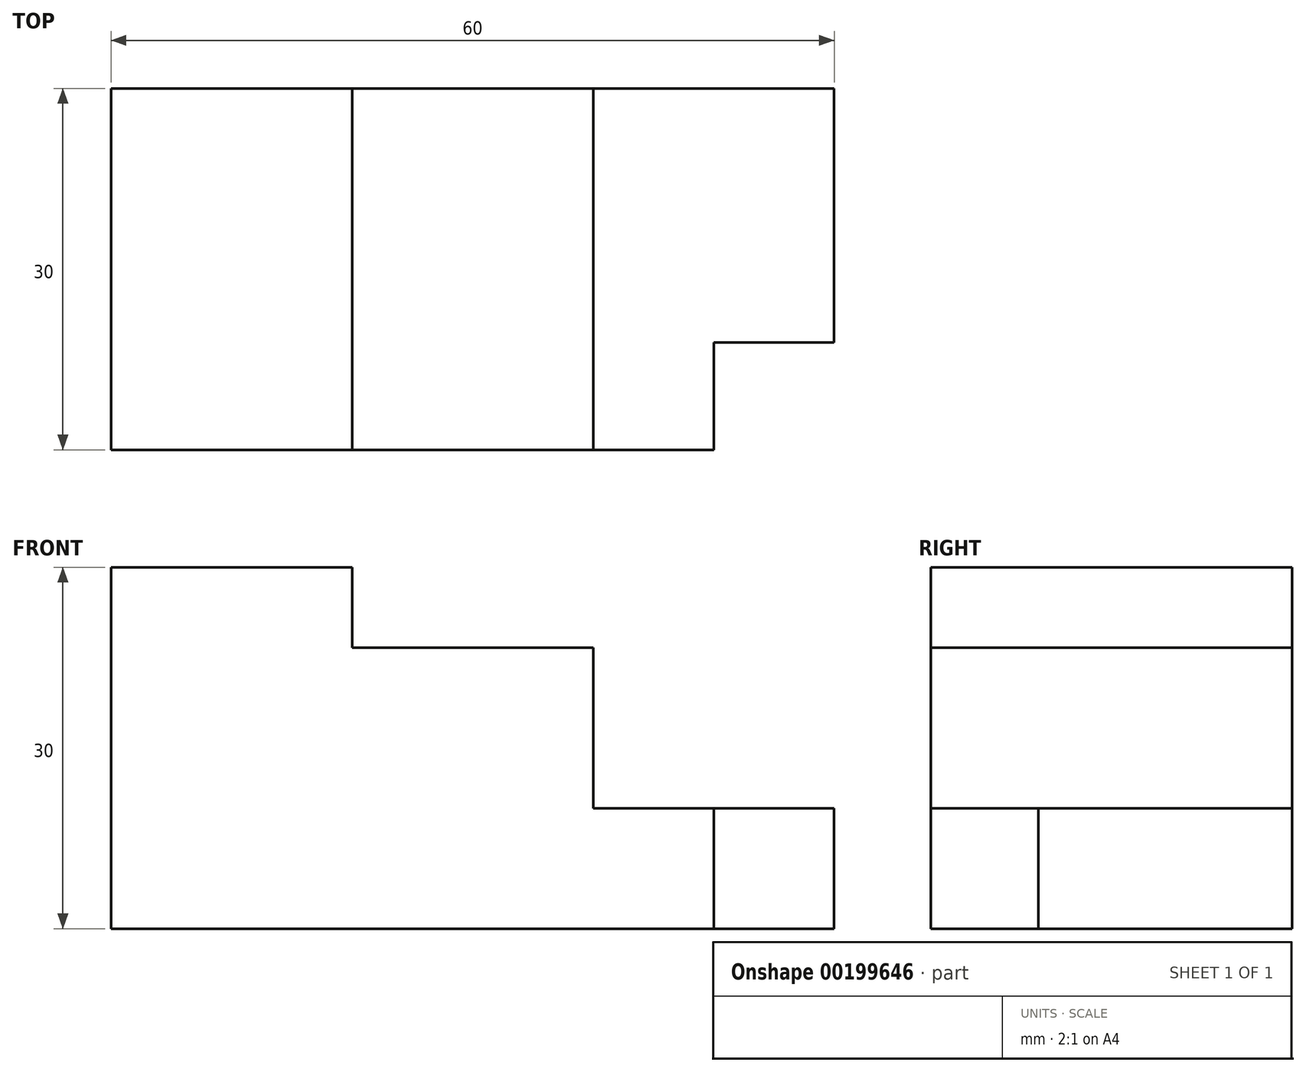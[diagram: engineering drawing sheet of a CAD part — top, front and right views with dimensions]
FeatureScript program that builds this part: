
annotation { "Feature Type Name" : "Feature", "Feature Type Description" : "" }
export const myFeature = defineFeature(function(context is Context, id is Id, definition is map)
    precondition{}
    {
        {
            var Q0;
            Q0=qCreatedBy(makeId("Front.planeOp"),FACE);
            var sketch = newSketch(context, id + "F0", { "sketchPlane" : qUnion([Q0])});
            skLineSegment(sketch, "E0", {"start": v(-31.94, 0) * mm, "end": v(-31.94, 30) * mm});
            skLineSegment(sketch, "E1", {"start": v(-31.94, 30) * mm, "end": v(-11.94, 30) * mm});
            skLineSegment(sketch, "E2", {"start": v(-11.94, 30) * mm, "end": v(-11.94, 23.33) * mm});
            skLineSegment(sketch, "E3", {"start": v(-11.94, 23.33) * mm, "end": v(8.06, 23.33) * mm});
            skLineSegment(sketch, "E4", {"start": v(8.06, 23.33) * mm, "end": v(8.06, 10) * mm});
            skLineSegment(sketch, "E5", {"start": v(8.06, 10) * mm, "end": v(28.06, 10) * mm});
            skLineSegment(sketch, "E6", {"start": v(28.06, 10) * mm, "end": v(28.06, 0) * mm});
            skLineSegment(sketch, "E7", {"start": v(28.06, 0) * mm, "end": v(-31.94, 0) * mm});
            skSolve(sketch);
        }
        {
            var Q0;
            Q0=makeQuery(id+"F0.imprint","IMPRINT",FACE,{"disambiguationData":[TD([[makeQuery(id+"F0.imprint","IMPRINT",EDGE,{"derivedFrom":sQuery(id+"F0.wireOp",EDGE,"E0")}),-1.0]])]});
            extrude(context, id + "F1", {"entities" : qUnion([Q0]), "depth" : 30 * mm});
        }
        {
            var Q0;
            Q0=makeQuery(id+"F1.opExtrude","SWEPT_FACE",FACE,{"disambiguationData":[OSD([sQuery(id+"F0.wireOp",EDGE,"E5")])]});
            var sketch = newSketch(context, id + "F2", { "sketchPlane" : qUnion([Q0])});
            skLineSegment(sketch, "E8.bottom", {"start": v(28.06, -30) * mm, "end": v(18.06, -30) * mm});
            skLineSegment(sketch, "E8.top", {"start": v(28.06, -21.08) * mm, "end": v(18.06, -21.08) * mm});
            skLineSegment(sketch, "E8.left", {"start": v(28.06, -30) * mm, "end": v(28.06, -21.08) * mm});
            skLineSegment(sketch, "E8.right", {"start": v(18.06, -30) * mm, "end": v(18.06, -21.08) * mm});
            skSolve(sketch);
        }
        {
            var Q0;
            Q0=makeQuery(id+"F2.imprint","IMPRINT",FACE,{"disambiguationData":[TD([[makeQuery(id+"F2.imprint","IMPRINT",EDGE,{"derivedFrom":sQuery(id+"F2.wireOp",EDGE,"E8.bottom")}),1.0]])]});
            extrude(context, id + "F3", {"entities" : qUnion([Q0]), "operationType" : NewBodyOperationType.REMOVE, "oppositeDirection" : true, "depth" : 25 * mm});
        }
    });
